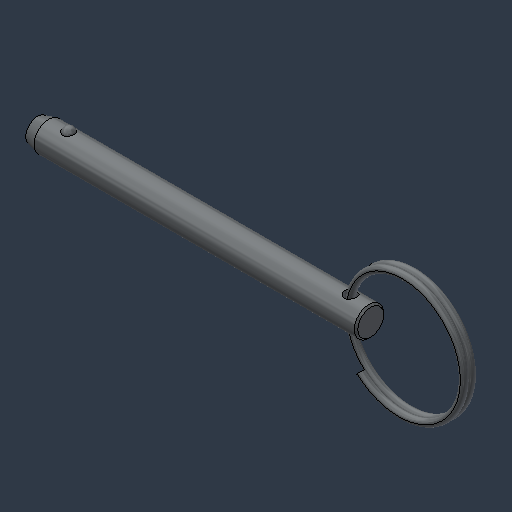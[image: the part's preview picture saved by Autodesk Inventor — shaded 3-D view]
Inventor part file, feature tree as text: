
AUTODESK INVENTOR PART (.ipt)
format: ipt  version: 2024.3 (Build 283343000, 343)  size: 219,136 bytes
history: native  units: mm (DEFAULTED — no unit token found)
features: revolve x1, other x1, sweep x1
ambient origin geometry x8: Origin, YZ Plane, XZ Plane, XY Plane, X Axis, Y Axis, Z Axis, Center Point
bodies: Solid1 (feature_tree), Solid2 (feature_tree), Solid3 (feature_tree)
feature tree (3):
  revolve  "Revolve2"  [1 undecoded]
  other  "Cut-Revolve2"
  sweep  "Sweep2"
note: 1 required parameter value undecoded (feature->parameter linkage not recoverable at this tier; creation-order binding heuristic only, values carry confidence <= 0.55)
